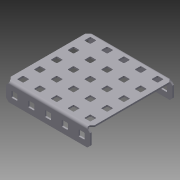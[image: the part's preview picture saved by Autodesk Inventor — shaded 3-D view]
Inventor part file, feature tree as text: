
AUTODESK INVENTOR PART (.ipt)
format: ipt  version: 2014 (Build 180170000, 170)  size: 1,321,472 bytes
history: native  units: in
note: dims shown in document units (in); Inventor stores cm internally (conversion verified against a paired STEP export)
features: extrude x2, sketch x2, other x1, imported_body x1
ambient origin geometry x8: Origin, YZ Plane, XZ Plane, XY Plane, X Axis, Y Axis, Z Axis, Center Point
bodies: Body1 (feature_tree)
feature tree (6):
  parser-record x1  (decoder bookkeeping rows leaked as tree rows — omitted from the tree; the rows remain in map.json)
  imported_body  "Base1"
  extrude  "Extrusion1"  Depth=1.0in TaperAngle=0.0deg
  extrude  "Extrusion2"  [1 undecoded]
  sketch  "Sketch1"  dims[d0=1.0in d1=0.0in d2=1.0in d3=0.0in]
  sketch  "Sketch2"
note: 1 required parameter value undecoded (feature->parameter linkage not recoverable at this tier; creation-order binding heuristic only, values carry confidence <= 0.55)
